# Revit family: BuzziShield Desk
name_source: partatom
category: Furniture
revit_build: Autodesk Revit 2018 (Build: 20190510_1515(x64)
units: mm (PartAtom-declared; Revit-internal decimal feet)

## family parameters
Always vertical = Yes
Cut with Voids When Loaded = No
OmniClass Number = 23.40.20.00
OmniClass Title = General Furniture and Specialties
Room Calculation Point = No
Shared = No
Work Plane-Based = No

## types (24) — shared parameters

## per-type parameters (varying)
| type | Fix Type | Length | Panel Type |
| 40cm x 60cm Foot | Fix : Foot | 1' - 11 5/8" | Panel : 40cm x 60cm |
| 40cm x 100cm Foot | Fix : Foot | 3' - 3 3/8" | Panel : 40cm x 100cm |
| 40cm x 140cm Foot | Fix : Foot | 4' - 7 1/8" | Panel : 40cm x 140cm |
| 60cm x 60cm Foot | Fix : Foot | 1' - 11 5/8" | Panel : 60cm x 60cm |
| 60cm x 100cm Foot | Fix : Foot | 3' - 3 3/8" | Panel : 60cm x 100cm |
| 60cm x 140cm Foot | Fix : Foot | 4' - 7 1/8" | Panel : 60cm x 140cm |
| 60cm x 60cm L | Fix : L Worktop | 1' - 11 5/8" | Panel : 60cm x 60cm |
| 60cm x 100cm L | Fix : L Worktop | 3' - 3 3/8" | Panel : 60cm x 100cm |
| 60cm x 100cm L Plus | Fix : L Plus Worktop | 3' - 3 3/8" | Panel : 60cm x 100cm |
| 60cm x 60cm L Plus | Fix : L Plus Worktop | 1' - 11 5/8" | Panel : 60cm x 60cm |
| 60cm x 60cm XL | Fix : XL Worktop | 1' - 11 5/8" | Panel : 60cm x 60cm |
| 60cm x 100cm XL | Fix : XL Worktop | 3' - 3 3/8" | Panel : 60cm x 100cm |
| 60cm x 140cm L | Fix : L Worktop | 4' - 7 1/8" | Panel : 60cm x 140cm |
| 60cm x 140cm L Plus | Fix : L Plus Worktop | 4' - 7 1/8" | Panel : 60cm x 140cm |
| 60cm x 140cm XL | Fix : XL Worktop | 4' - 7 1/8" | Panel : 60cm x 140cm |
| 40cm x 60cm L | Fix : L Worktop | 1' - 11 5/8" | Panel : 40cm x 60cm |
| 40cm x 60cm L Plus | Fix : L Plus Worktop | 1' - 11 5/8" | Panel : 40cm x 60cm |
| 40cm x 60cm XL | Fix : XL Worktop | 1' - 11 5/8" | Panel : 40cm x 60cm |
| 40cm x 100cm L | Fix : L Worktop | 3' - 3 3/8" | Panel : 40cm x 100cm |
| 40cm x 100cm L Plus | Fix : L Plus Worktop | 3' - 3 3/8" | Panel : 40cm x 100cm |
| 40cm x 100cm XL | Fix : XL Worktop | 3' - 3 3/8" | Panel : 40cm x 100cm |
| 40cm x 140cm L | Fix : L Worktop | 4' - 7 1/8" | Panel : 40cm x 140cm |
| 40cm x 140cm L Plus | Fix : L Plus Worktop | 4' - 7 1/8" | Panel : 40cm x 140cm |
| 40cm x 140cm XL | Fix : XL Worktop | 4' - 7 1/8" | Panel : 40cm x 140cm |

## geometry (parser evidence)
native form markers: Sweep x7
no freeform markers — native parametric forms only
